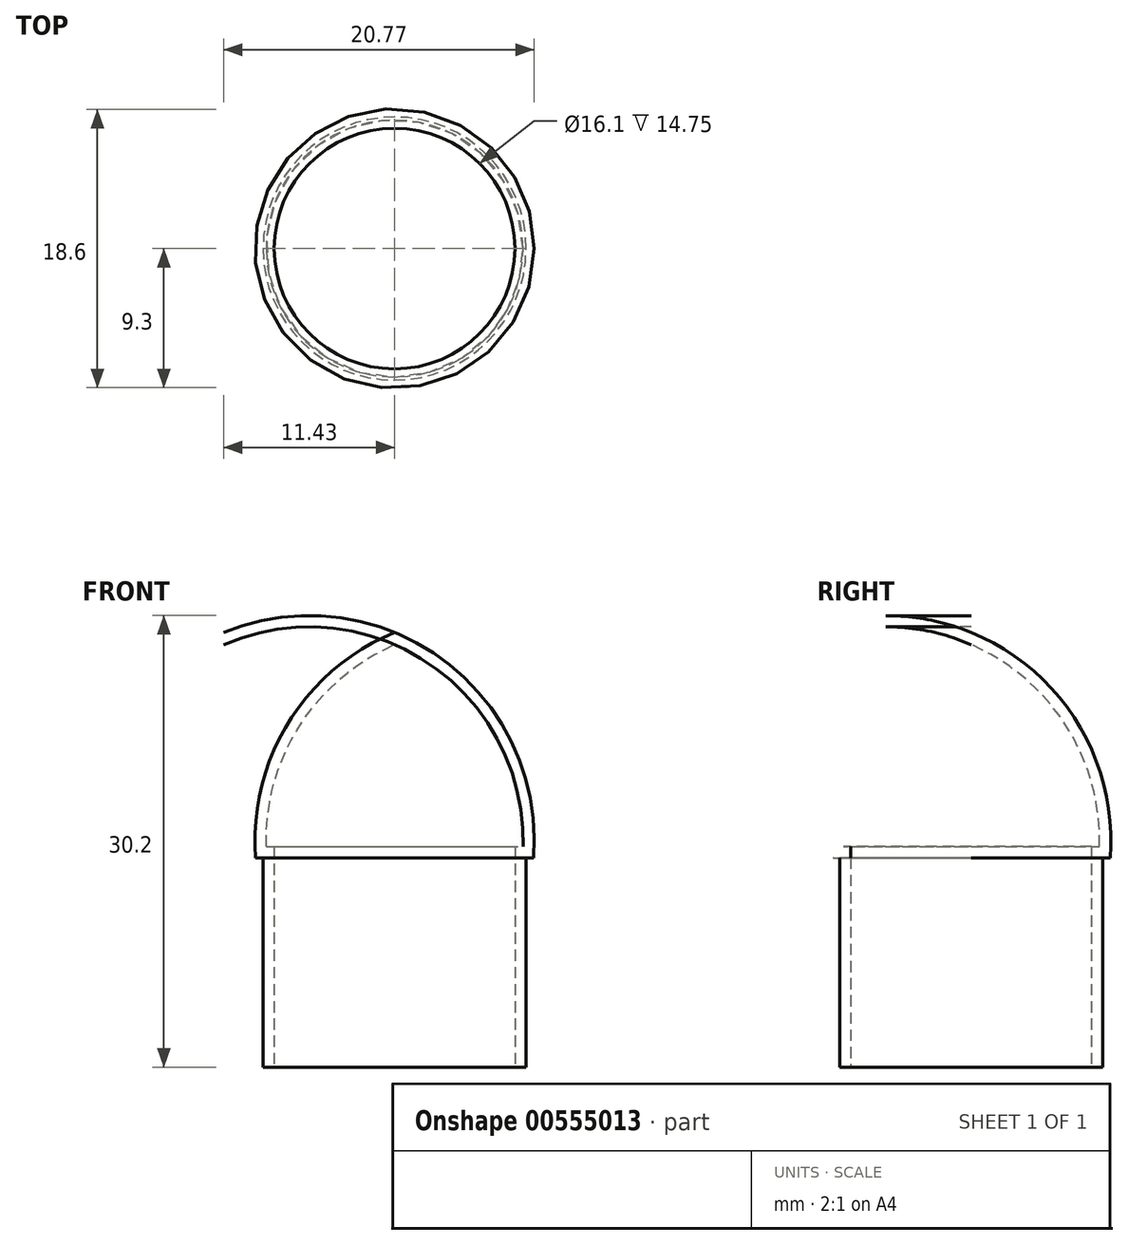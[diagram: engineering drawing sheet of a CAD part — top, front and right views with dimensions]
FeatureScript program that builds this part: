
annotation { "Feature Type Name" : "Feature", "Feature Type Description" : "" }
export const myFeature = defineFeature(function(context is Context, id is Id, definition is map)
    precondition{}
    {
        {
            var Q0;
            Q0=qCreatedBy(makeId("Front.planeOp"),FACE);
            var sketch = newSketch(context, id + "F0", { "sketchPlane" : qUnion([Q0])});
            skLineSegment(sketch, "E0", {"start": v(0, 0) * mm, "end": v(0, 30) * mm});
            skLineSegment(sketch, "E1", {"start": v(8.05, 0.93) * mm, "end": v(8.05, 15.68) * mm});
            skLineSegment(sketch, "E2", {"start": v(8.05, 15.68) * mm, "end": v(8.59, 15.68) * mm});
            skArc(sketch, "E3", {"start": v(8.59, 15.68) * mm, "mid": v(6.36, 23.75) * mm, "end": v(0, 29.19) * mm});
            skArc(sketch, "E4.0", {"start": v(9.3, 14.93) * mm, "mid": v(7.1, 23.98) * mm, "end": v(0, 30) * mm});
            skLineSegment(sketch, "E4.1", {"start": v(8.8, 14.93) * mm, "end": v(9.3, 14.93) * mm});
            skLineSegment(sketch, "E4.2", {"start": v(8.8, 0.93) * mm, "end": v(8.8, 14.93) * mm});
            skLineSegment(sketch, "E5", {"start": v(8.05, 0.93) * mm, "end": v(8.8, 0.93) * mm});
            skLineSegment(sketch, "E6", {"start": v(0, -2.38) * mm, "end": v(0, 0) * mm});
            skSolve(sketch);
        }
        {
            var Q0;
            Q0=makeQuery(id+"F0.imprint","IMPRINT",FACE,{"disambiguationData":[TD([[makeQuery(id+"F0.imprint","IMPRINT",EDGE,{"derivedFrom":sQuery(id+"F0.wireOp",EDGE,"E1")}),-1.0]])]});
            var Q1;
            Q1=sQuery(id+"F0.wireOp",EDGE,"E0");
            revolve(context, id + "F1", {"entities" : qUnion([Q0]), "axis" : qUnion([Q1]), "revolveType" : RevolveType.FULL});
        }
    });
